# Revit family: 101010004202804
name_source: partatom
category: Modelos genéricos
units: mm (PartAtom-declared; Revit-internal decimal feet)

## family parameters
Compartido = No
Corte con vacíos al cargar = No
Cota de conector redondo = Diámetro de uso
Puede alojar armadura = No
Punto de cálculo de habitación = No
Se basa en plano de trabajo = No
Siempre vertical = No
Tipo de pieza = Normal

## types (1)
- SEPARADOR MOLDAJE T MUELA BOLSA 1.000UN
    Aplicacion = Se aplican en forma horizontal sobre el encofrado o placa fenólica dejando reposar la barra sobre esta. (4 Un. x m2 Aprox.)
    Color = Negro
    Descripción = Se usa para distanciar una barra o malla, del encofrado o fenólico.
    Dimension = 20 mm  [stored 0.0656168 ft]
    Empresa = CNP SPA.
    Espesor = 0 mm  [stored 0 ft]
    Material = PEAD
    Modelo = SEPARADOR MOLDAJE T MUELA
    Nombre SKU = SEPARADOR MOLDAJE T MUELA BOLSA 1.000UN
    Num SKUs = 101010004202804
    URL = https://www.empresascnp.cl
    Unidad = Bolsa 1000 Un.
    Url Ficha tecnica = https://empresascnp.cl
    Uso = Para distanciar una barra o malla, del encofrado o fenólico. Para fierros de 12 a 20mm. Con recubrimientos de 12, 15, 17 y 20mm.
    Ventajas = Fácil de instalar, permite dos posiciones en una pieza, ayuda a mantener los espesores de hormigón según cálculo, se eliminan gran cantidad de fisuras que se producen por un irregular trabajo del hormigón /acero.

note: [stored X ft] marks values corroborated as IEEE doubles in the binary element streams (Revit-internal decimal feet)

## geometry (parser evidence)
native form markers: Sweep x2
no freeform markers — native parametric forms only
